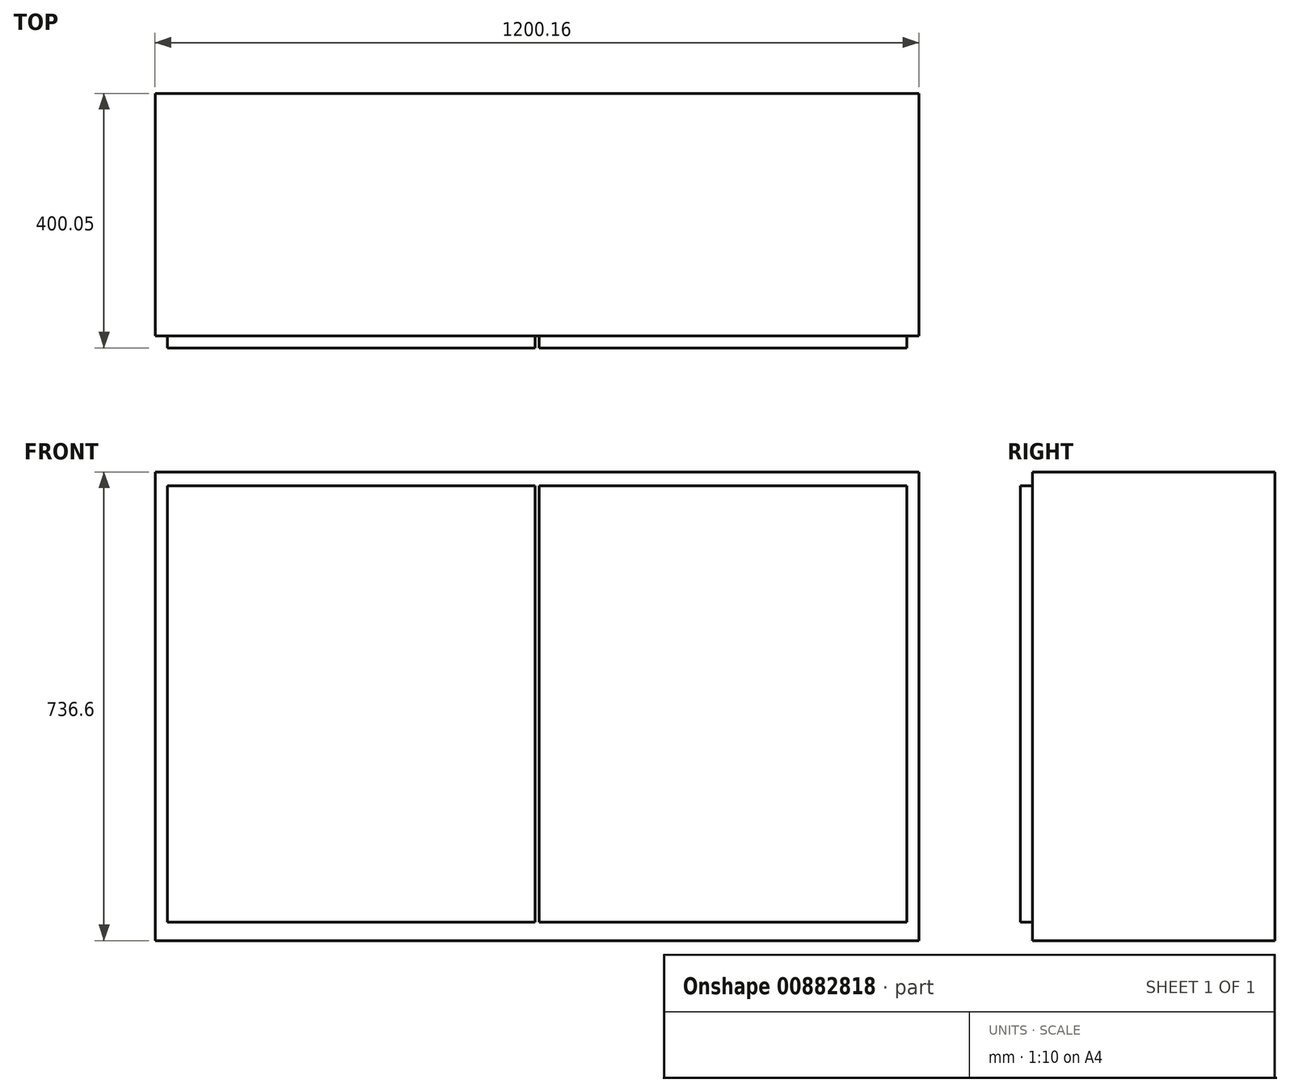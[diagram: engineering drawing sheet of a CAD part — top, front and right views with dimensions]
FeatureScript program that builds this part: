
annotation { "Feature Type Name" : "Feature", "Feature Type Description" : "" }
export const myFeature = defineFeature(function(context is Context, id is Id, definition is map)
    precondition{}
    {
        {
            var Q0;
            Q0=qCreatedBy(makeId("Front.planeOp"),FACE);
            var sketch = newSketch(context, id + "F0", { "sketchPlane" : qUnion([Q0])});
            skLineSegment(sketch, "E0.bottom", {"start": v(600.07, 368.3) * mm, "end": v(-600.08, 368.3) * mm});
            skLineSegment(sketch, "E0.top", {"start": v(600.08, -368.3) * mm, "end": v(-600.07, -368.3) * mm});
            skLineSegment(sketch, "E0.left", {"start": v(600.07, 368.3) * mm, "end": v(600.08, -368.3) * mm});
            skLineSegment(sketch, "E0.right", {"start": v(-600.08, 368.3) * mm, "end": v(-600.07, -368.3) * mm});
            skPoint(sketch, "E0.middle", {"position": v(0, 0) * mm});
            skSolve(sketch);
        }
        {
            var Q0;
            Q0 = qSketchRegion(id + "F0", true);
            extrude(context, id + "F1", {"entities" : qUnion([Q0]), "depth" : 381 * mm, "offsetDistance" : 25.4 * mm});
        }
        {
            var Q0;
            Q0=makeQuery(id+"F1.opExtrude","CAP_FACE",FACE,{"disambiguationData":[OSD([sQuery(id+"F0.wireOp",EDGE,"E0.bottom"),sQuery(id+"F0.wireOp",EDGE,"E0.top"),sQuery(id+"F0.wireOp",EDGE,"E0.left"),sQuery(id+"F0.wireOp",EDGE,"E0.right")])],"isStart":false});
            var sketch = newSketch(context, id + "F2", { "sketchPlane" : qUnion([Q0])});
            skLineSegment(sketch, "E1.bottom", {"start": v(-581.02, -339.32) * mm, "end": v(-3.17, -339.32) * mm});
            skLineSegment(sketch, "E1.top", {"start": v(-581.02, 346.48) * mm, "end": v(-3.17, 346.48) * mm});
            skLineSegment(sketch, "E2.1.0.0", {"start": v(3.18, -339.32) * mm, "end": v(581.03, -339.32) * mm});
            skLineSegment(sketch, "E2.1.0.2", {"start": v(3.18, 346.48) * mm, "end": v(581.03, 346.48) * mm});
            skLineSegment(sketch, "E2.direction1", {"start": v(-581.02, -339.32) * mm, "end": v(3.18, -339.32) * mm, "construction": true});
            skLineSegment(sketch, "E3", {"start": v(-581.02, 346.48) * mm, "end": v(-581.02, -339.32) * mm});
            skLineSegment(sketch, "E4", {"start": v(581.03, 346.48) * mm, "end": v(581.03, -339.32) * mm});
            skLineSegment(sketch, "E5", {"start": v(-3.17, 346.48) * mm, "end": v(-3.17, -339.32) * mm});
            skLineSegment(sketch, "E6", {"start": v(3.18, 346.48) * mm, "end": v(3.18, -339.32) * mm});
            skSolve(sketch);
        }
        {
            var Q0;
            Q0 = qSketchRegion(id + "F2", true);
            extrude(context, id + "F3", {"entities" : qUnion([Q0]), "operationType" : NewBodyOperationType.ADD, "depth" : 19.05 * mm, "offsetDistance" : 25.4 * mm});
        }
    });
